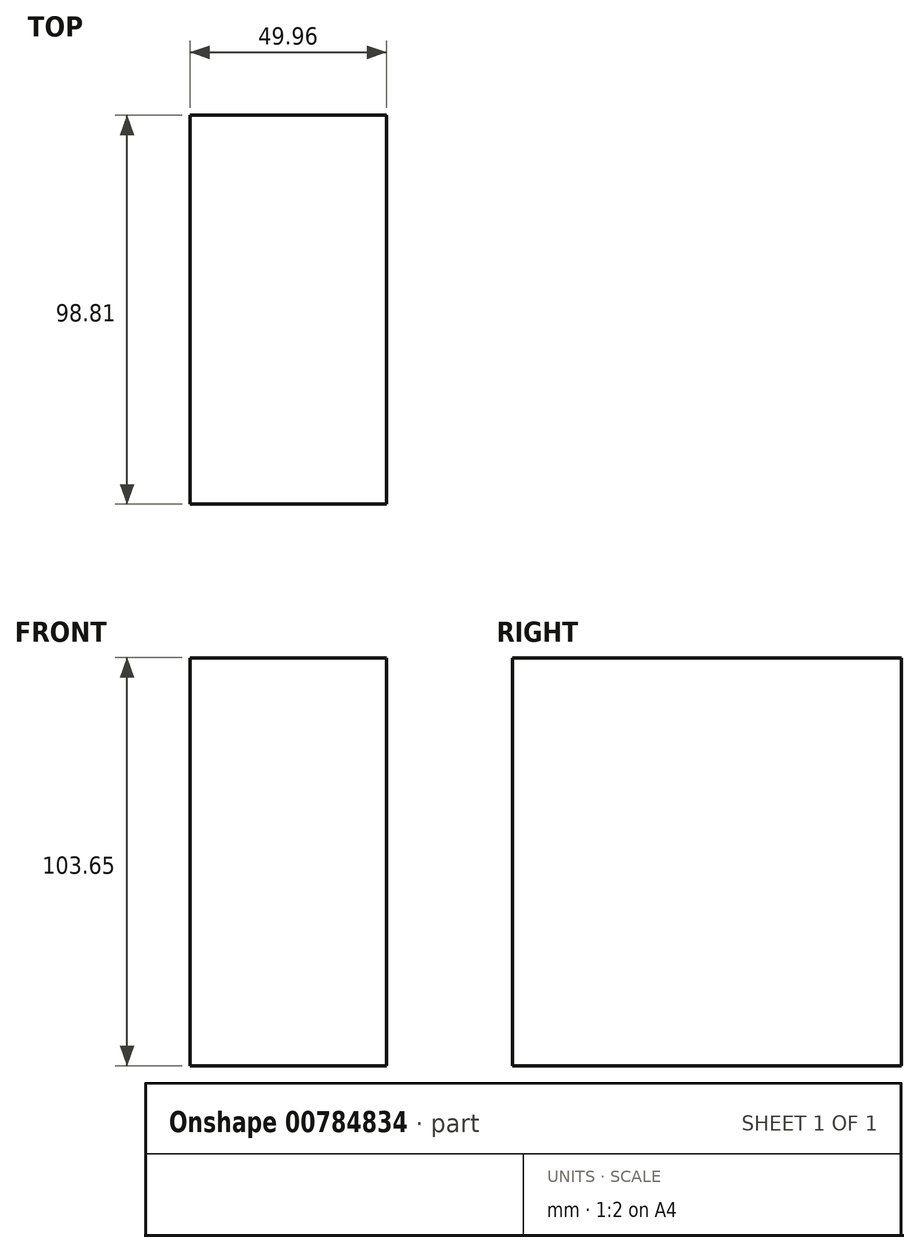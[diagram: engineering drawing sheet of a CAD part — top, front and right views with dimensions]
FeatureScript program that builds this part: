
annotation { "Feature Type Name" : "Feature", "Feature Type Description" : "" }
export const myFeature = defineFeature(function(context is Context, id is Id, definition is map)
    precondition{}
    {
        {
            var Q0;
            Q0=qCreatedBy(makeId("Front.planeOp"),FACE);
            var sketch = newSketch(context, id + "F0", { "sketchPlane" : qUnion([Q0])});
            skLineSegment(sketch, "E0.bottom", {"start": v(-26.94, 28.83) * mm, "end": v(53.5, 28.83) * mm});
            skLineSegment(sketch, "E0.top", {"start": v(-26.94, -23.67) * mm, "end": v(53.5, -23.67) * mm});
            skLineSegment(sketch, "E0.left", {"start": v(-26.94, 28.83) * mm, "end": v(-26.94, -23.67) * mm});
            skLineSegment(sketch, "E0.right", {"start": v(53.5, 28.83) * mm, "end": v(53.5, -23.67) * mm});
            skLineSegment(sketch, "E1.bottom", {"start": v(53.5, -23.67) * mm, "end": v(103.45, -23.67) * mm});
            skLineSegment(sketch, "E1.top", {"start": v(53.5, 79.98) * mm, "end": v(103.45, 79.98) * mm});
            skLineSegment(sketch, "E1.left", {"start": v(53.5, -23.67) * mm, "end": v(53.5, 79.98) * mm});
            skLineSegment(sketch, "E1.right", {"start": v(103.45, -23.67) * mm, "end": v(103.45, 79.98) * mm});
            skSolve(sketch);
        }
        {
            var Q0;
            {var subQ3=sQuery(id+"F0.wireOp",EDGE,"E1.bottom");Q0=makeQuery(id+"F0.imprint","IMPRINT",FACE,{"disambiguationData":[TD([[makeQuery(id+"F0.imprint","IMPRINT",EDGE,{"derivedFrom":subQ3}),1.0]])]});}
            extrude(context, id + "F1", {"entities" : qUnion([Q0]), "depth" : 98.8 * mm, "offsetDistance" : 25.4 * mm});
        }
    });
